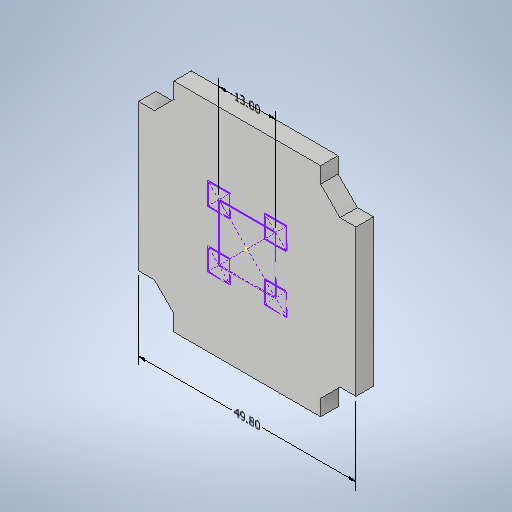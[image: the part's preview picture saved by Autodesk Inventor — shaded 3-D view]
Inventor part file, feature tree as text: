
AUTODESK INVENTOR PART (.ipt)
format: ipt  version: 2025.1 (Build 291241000, 241)  size: 266,752 bytes
history: native  units: mm
features: sketch x2, other x2, extrude x1
ambient origin geometry x8: Origin, YZ Plane, XZ Plane, XY Plane, X Axis, Y Axis, Z Axis, Center Point
bodies: 实体1 (feature_tree)
feature tree (5):
  extrude  "拉伸1"  [1 undecoded]
  sketch  "草图2"  dims[d45=5.895245mm d46=4.635271mm d47=13.0mm d48=4.756255mm d49=5.78255mm d50=49.801261mm]
  sketch  "草图1"  dims[d31=4.0mm d32=0.0mm]
  other  "线性尺寸 1"
  other  "线性尺寸 2"
note: 1 required parameter value undecoded (feature->parameter linkage not recoverable at this tier; creation-order binding heuristic only, values carry confidence <= 0.55)
